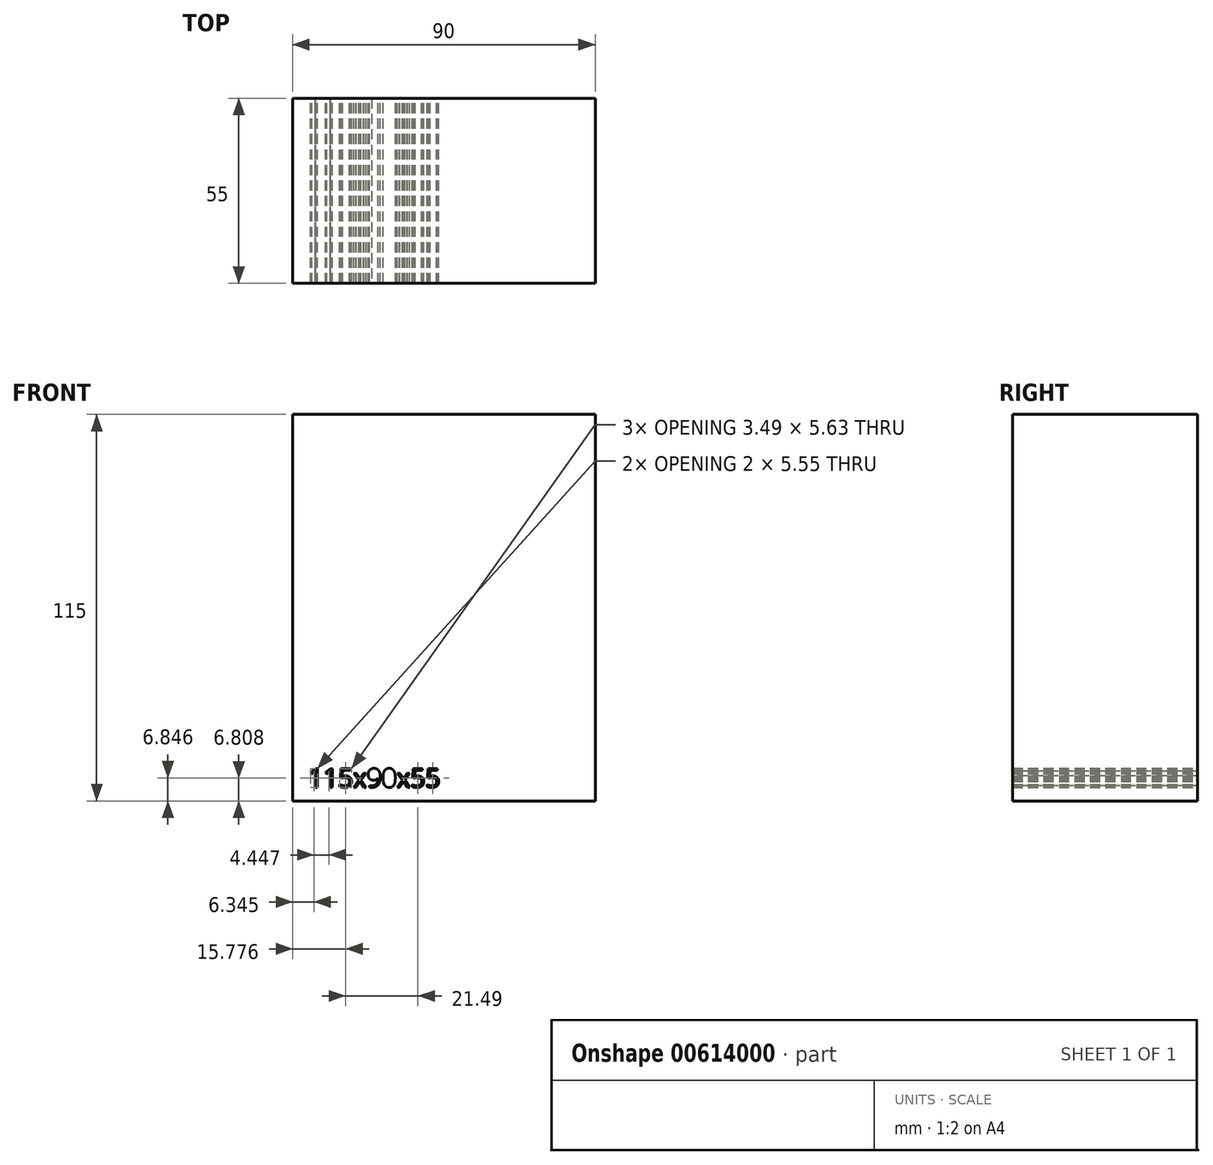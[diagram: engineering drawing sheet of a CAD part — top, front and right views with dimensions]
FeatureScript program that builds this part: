
annotation { "Feature Type Name" : "Feature", "Feature Type Description" : "" }
export const myFeature = defineFeature(function(context is Context, id is Id, definition is map)
    precondition{}
    {
        {
            var Q0;
            Q0=qCreatedBy(makeId("Front.planeOp"),FACE);
            var sketch = newSketch(context, id + "F0", { "sketchPlane" : qUnion([Q0])});
            skLineSegment(sketch, "E0.bottom", {"start": v(-45, 57.5) * mm, "end": v(45, 57.5) * mm});
            skLineSegment(sketch, "E0.top", {"start": v(-45, -57.5) * mm, "end": v(45, -57.5) * mm});
            skLineSegment(sketch, "E0.left", {"start": v(-45, 57.5) * mm, "end": v(-45, -57.5) * mm});
            skLineSegment(sketch, "E0.right", {"start": v(45, 57.5) * mm, "end": v(45, -57.5) * mm});
            skPoint(sketch, "E0.middle", {"position": v(0, 0) * mm});
            skText(sketch, "E1", { "text": "115x90x55\n", "fontName": "OpenSans-Regular.ttf"});
            const initialGuessF0  = {"E1": [-0.04037, -0.05343, 1, 0, 0.0056]};
            skSetInitialGuess(sketch, initialGuessF0);
            skSolve(sketch);
        }
        {
            var Q0;
            Q0=makeQuery(id+"F0.imprint","IMPRINT",FACE,{"disambiguationData":[TD([[makeQuery(id+"F0.imprint","IMPRINT",EDGE,{"derivedFrom":sQuery(id+"F0.wireOp",EDGE,"E0.bottom")}),-1.0]])]});
            extrude(context, id + "F1", {"entities" : qUnion([Q0]), "depth" : 55 * mm, "offsetDistance" : 25 * mm});
        }
    });
